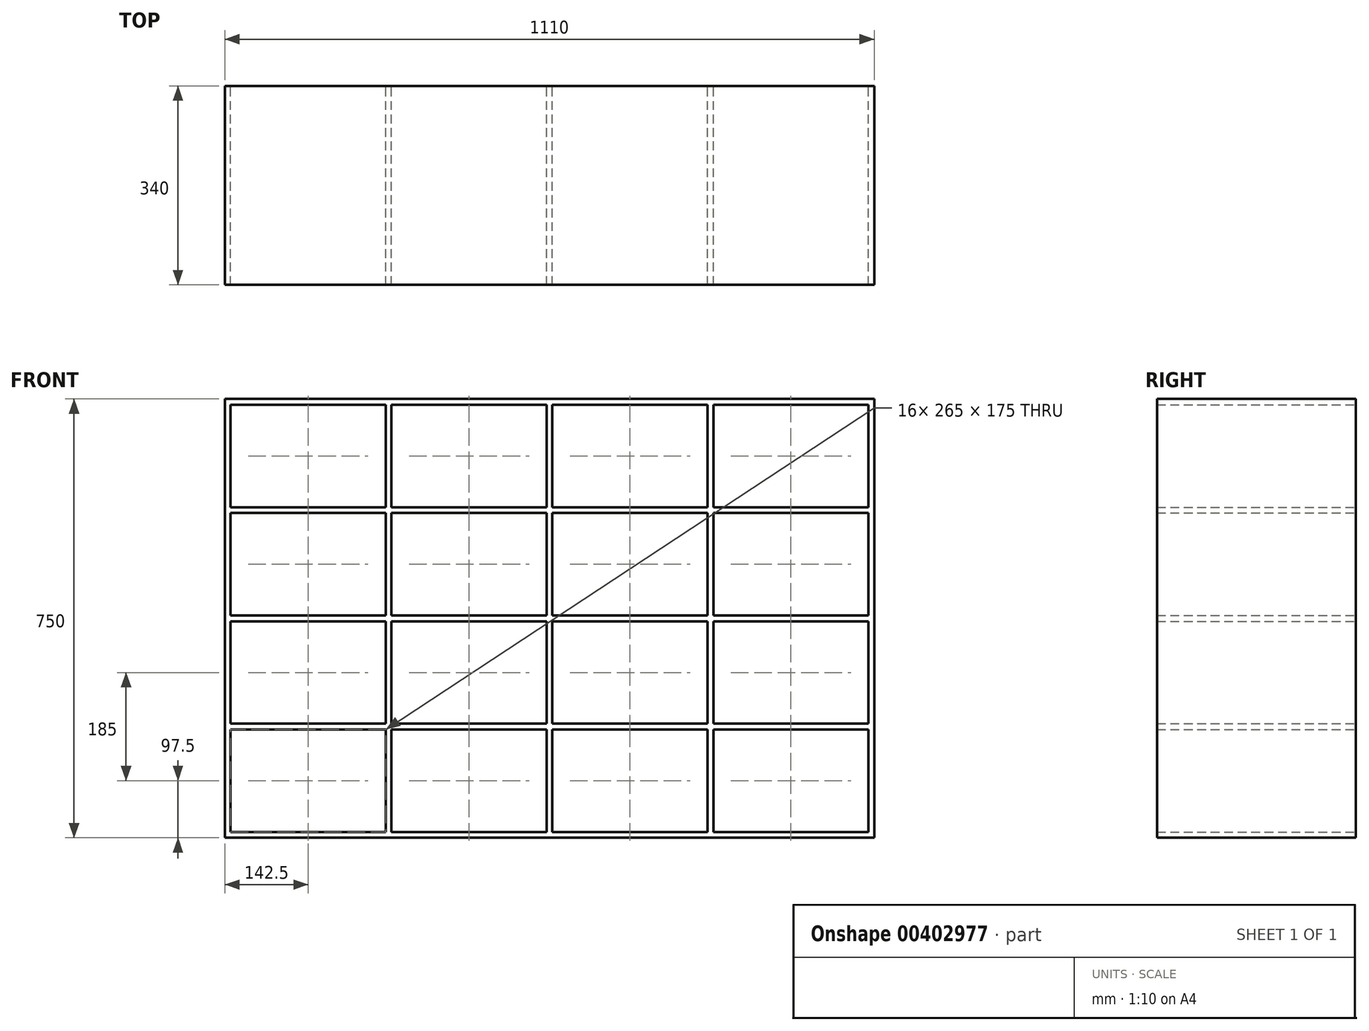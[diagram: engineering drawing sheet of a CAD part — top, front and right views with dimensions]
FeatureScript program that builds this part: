
annotation { "Feature Type Name" : "Feature", "Feature Type Description" : "" }
export const myFeature = defineFeature(function(context is Context, id is Id, definition is map)
    precondition{}
    {
        {
            var Q0;
            Q0=qCreatedBy(makeId("Front.planeOp"),FACE);
            var sketch = newSketch(context, id + "F0", { "sketchPlane" : qUnion([Q0])});
            skLineSegment(sketch, "E0.bottom", {"start": v(-555, 375) * mm, "end": v(555, 375) * mm});
            skLineSegment(sketch, "E0.top", {"start": v(-555, -375) * mm, "end": v(555, -375) * mm});
            skLineSegment(sketch, "E0.left", {"start": v(-555, 375) * mm, "end": v(-555, -375) * mm});
            skLineSegment(sketch, "E0.right", {"start": v(555, 375) * mm, "end": v(555, -375) * mm});
            skPoint(sketch, "E0.middle", {"position": v(0, 0) * mm});
            skLineSegment(sketch, "E1.bottom", {"start": v(-545, 365) * mm, "end": v(-280, 365) * mm});
            skLineSegment(sketch, "E1.top", {"start": v(-545, -365) * mm, "end": v(-280, -365) * mm});
            skLineSegment(sketch, "E1.left", {"start": v(-545, 365) * mm, "end": v(-545, 190) * mm});
            skLineSegment(sketch, "E1.right", {"start": v(545, 365) * mm, "end": v(545, 190) * mm});
            skLineSegment(sketch, "E2", {"start": v(-280, 365) * mm, "end": v(-280, 190) * mm});
            skLineSegment(sketch, "E3", {"start": v(-270, 365) * mm, "end": v(-270, 190) * mm});
            skLineSegment(sketch, "E4", {"start": v(-5, 365) * mm, "end": v(-5, 190) * mm});
            skLineSegment(sketch, "E5", {"start": v(5, -365) * mm, "end": v(5, -190) * mm});
            skLineSegment(sketch, "E6", {"start": v(270, -365) * mm, "end": v(270, -190) * mm});
            skLineSegment(sketch, "E7", {"start": v(280, -365) * mm, "end": v(280, -190) * mm});
            skLineSegment(sketch, "E8.trimOffspring", {"start": v(-270, 365) * mm, "end": v(-5, 365) * mm});
            skLineSegment(sketch, "E9.trimOffspring", {"start": v(5, 365) * mm, "end": v(270, 365) * mm});
            skLineSegment(sketch, "E10.trimOffspring", {"start": v(280, 365) * mm, "end": v(545, 365) * mm});
            skLineSegment(sketch, "E11.trimOffspring", {"start": v(280, -365) * mm, "end": v(545, -365) * mm});
            skLineSegment(sketch, "E12.trimOffspring", {"start": v(5, -365) * mm, "end": v(270, -365) * mm});
            skLineSegment(sketch, "E13.trimOffspring", {"start": v(-270, -365) * mm, "end": v(-5, -365) * mm});
            skLineSegment(sketch, "E14", {"start": v(-545, -190) * mm, "end": v(-280, -190) * mm});
            skLineSegment(sketch, "E15", {"start": v(-545, -180) * mm, "end": v(-280, -180) * mm});
            skLineSegment(sketch, "E16", {"start": v(-545, 5) * mm, "end": v(-280, 5) * mm});
            skLineSegment(sketch, "E17", {"start": v(-545, -5) * mm, "end": v(-280, -5) * mm});
            skLineSegment(sketch, "E18", {"start": v(-545, 180) * mm, "end": v(-280, 180) * mm});
            skLineSegment(sketch, "E19", {"start": v(-545, 190) * mm, "end": v(-280, 190) * mm});
            skLineSegment(sketch, "E20.trimOffspring", {"start": v(-270, 190) * mm, "end": v(-5, 190) * mm});
            skLineSegment(sketch, "E21.trimOffspring", {"start": v(-270, 180) * mm, "end": v(-270, 5) * mm});
            skLineSegment(sketch, "E22.trimOffspring", {"start": v(-270, 180) * mm, "end": v(-5, 180) * mm});
            skLineSegment(sketch, "E23.trimOffspring", {"start": v(-280, 180) * mm, "end": v(-280, 5) * mm});
            skLineSegment(sketch, "E24.trimOffspring", {"start": v(-5, 180) * mm, "end": v(-5, 5) * mm});
            skLineSegment(sketch, "E25.trimOffspring", {"start": v(-270, -5) * mm, "end": v(-5, -5) * mm});
            skLineSegment(sketch, "E26.trimOffspring", {"start": v(-280, -5) * mm, "end": v(-280, -180) * mm});
            skLineSegment(sketch, "E27.trimOffspring", {"start": v(-270, 5) * mm, "end": v(-5, 5) * mm});
            skLineSegment(sketch, "E28.trimOffspring", {"start": v(-270, -5) * mm, "end": v(-270, -180) * mm});
            skLineSegment(sketch, "E29.trimOffspring", {"start": v(-270, -180) * mm, "end": v(-5, -180) * mm});
            skLineSegment(sketch, "E30.trimOffspring", {"start": v(-280, -190) * mm, "end": v(-280, -365) * mm});
            skLineSegment(sketch, "E31.trimOffspring", {"start": v(-270, -190) * mm, "end": v(-5, -190) * mm});
            skLineSegment(sketch, "E32.trimOffspring", {"start": v(-270, -190) * mm, "end": v(-270, -365) * mm});
            skLineSegment(sketch, "E33.trimOffspring", {"start": v(-545, -190) * mm, "end": v(-545, -365) * mm});
            skLineSegment(sketch, "E34.trimOffspring", {"start": v(-545, -5) * mm, "end": v(-545, -180) * mm});
            skLineSegment(sketch, "E35.trimOffspring", {"start": v(-545, 180) * mm, "end": v(-545, 5) * mm});
            skLineSegment(sketch, "E36.trimOffspring", {"start": v(5, 190) * mm, "end": v(270, 190) * mm});
            skLineSegment(sketch, "E37.trimOffspring", {"start": v(5, 190) * mm, "end": v(5, 365) * mm});
            skLineSegment(sketch, "E38.trimOffspring", {"start": v(5, 180) * mm, "end": v(270, 180) * mm});
            skLineSegment(sketch, "E39.trimOffspring", {"start": v(5, 5) * mm, "end": v(270, 5) * mm});
            skLineSegment(sketch, "E40.trimOffspring", {"start": v(5, 5) * mm, "end": v(5, 180) * mm});
            skLineSegment(sketch, "E41.trimOffspring", {"start": v(-5, -5) * mm, "end": v(-5, -180) * mm});
            skLineSegment(sketch, "E42.trimOffspring", {"start": v(5, -5) * mm, "end": v(270, -5) * mm});
            skLineSegment(sketch, "E43.trimOffspring", {"start": v(270, 190) * mm, "end": v(270, 365) * mm});
            skLineSegment(sketch, "E44.trimOffspring", {"start": v(280, 190) * mm, "end": v(545, 190) * mm});
            skLineSegment(sketch, "E45.trimOffspring", {"start": v(280, 180) * mm, "end": v(545, 180) * mm});
            skLineSegment(sketch, "E46.trimOffspring", {"start": v(545, 180) * mm, "end": v(545, 5) * mm});
            skLineSegment(sketch, "E47.trimOffspring", {"start": v(545, -5) * mm, "end": v(545, -180) * mm});
            skLineSegment(sketch, "E48.trimOffspring", {"start": v(545, -190) * mm, "end": v(545, -365) * mm});
            skLineSegment(sketch, "E49.trimOffspring", {"start": v(270, -180) * mm, "end": v(270, -5) * mm});
            skLineSegment(sketch, "E50.trimOffspring", {"start": v(280, -180) * mm, "end": v(545, -180) * mm});
            skLineSegment(sketch, "E51.trimOffspring", {"start": v(280, -180) * mm, "end": v(280, -5) * mm});
            skLineSegment(sketch, "E52.trimOffspring", {"start": v(280, -190) * mm, "end": v(545, -190) * mm});
            skLineSegment(sketch, "E53.trimOffspring", {"start": v(5, -180) * mm, "end": v(270, -180) * mm});
            skLineSegment(sketch, "E54.trimOffspring", {"start": v(5, -190) * mm, "end": v(270, -190) * mm});
            skLineSegment(sketch, "E55.trimOffspring", {"start": v(280, 5) * mm, "end": v(280, 180) * mm});
            skLineSegment(sketch, "E56.trimOffspring", {"start": v(280, 5) * mm, "end": v(545, 5) * mm});
            skLineSegment(sketch, "E57.trimOffspring", {"start": v(280, -5) * mm, "end": v(545, -5) * mm});
            skLineSegment(sketch, "E58.trimOffspring", {"start": v(270, 5) * mm, "end": v(270, 180) * mm});
            skLineSegment(sketch, "E59.trimOffspring", {"start": v(-5, -190) * mm, "end": v(-5, -365) * mm});
            skLineSegment(sketch, "E60.trimOffspring", {"start": v(5, -180) * mm, "end": v(5, -5) * mm});
            skLineSegment(sketch, "E61.trimOffspring", {"start": v(280, 190) * mm, "end": v(280, 365) * mm});
            skSolve(sketch);
        }
        {
            var Q0;
            Q0=makeQuery(id+"F0.imprint","IMPRINT",FACE,{"disambiguationData":[TD([[makeQuery(id+"F0.imprint","IMPRINT",EDGE,{"derivedFrom":sQuery(id+"F0.wireOp",EDGE,"E0.bottom")}),-1.0]])]});
            extrude(context, id + "F1", {"entities" : qUnion([Q0]), "endBound" : BoundingType.SYMMETRIC, "depth" : 340 * mm});
        }
    });
